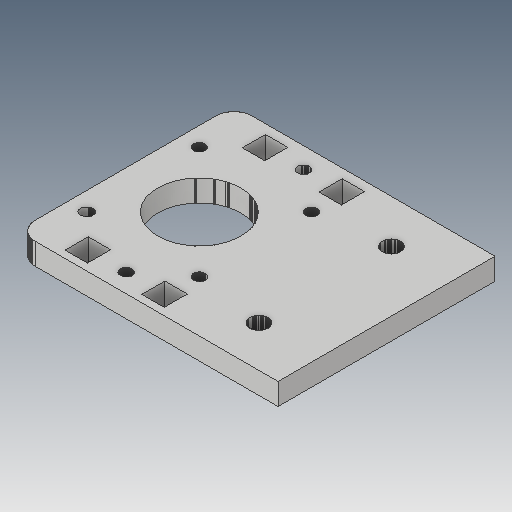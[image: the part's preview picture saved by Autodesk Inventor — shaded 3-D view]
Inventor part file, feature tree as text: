
AUTODESK INVENTOR PART (.ipt)
format: ipt  version: 2017 (Build 210142000, 142)  size: 1,142,784 bytes
history: native  units: mm
features: sketch x4, extrude x2, hole x2
ambient origin geometry x8: Origin, YZ Plane, XZ Plane, XY Plane, X Axis, Y Axis, Z Axis, Center Point
bodies: Solid1 (feature_tree)
feature tree (8):
  extrude  "Extrusion1"  Depth=10.0mm TaperAngle=0.0deg
  hole  "Hole1"  [1 undecoded]
  hole  "Hole2"  [1 undecoded]
  extrude  "Extrusion2"  [1 undecoded]
  sketch  "Sketch1"  dims[d0=6.0mm d1=0.0mm]
  sketch  "Sketch2"  dims[d2=3.2mm d3=6.0mm d4=4.0mm d5=2.0mm d6=90.0deg d7=8.0mm d8=20.594885mm]
  sketch  "Sketch3"  dims[d9=5.0mm d10=6.0mm d11=4.0mm d12=2.0mm d13=90.0deg d14=8.0mm d15=20.594885mm d16=10.0mm d17=0.0mm]
  sketch  "Sketch4"
note: 3 required parameter values undecoded (feature->parameter linkage not recoverable at this tier; creation-order binding heuristic only, values carry confidence <= 0.55)
